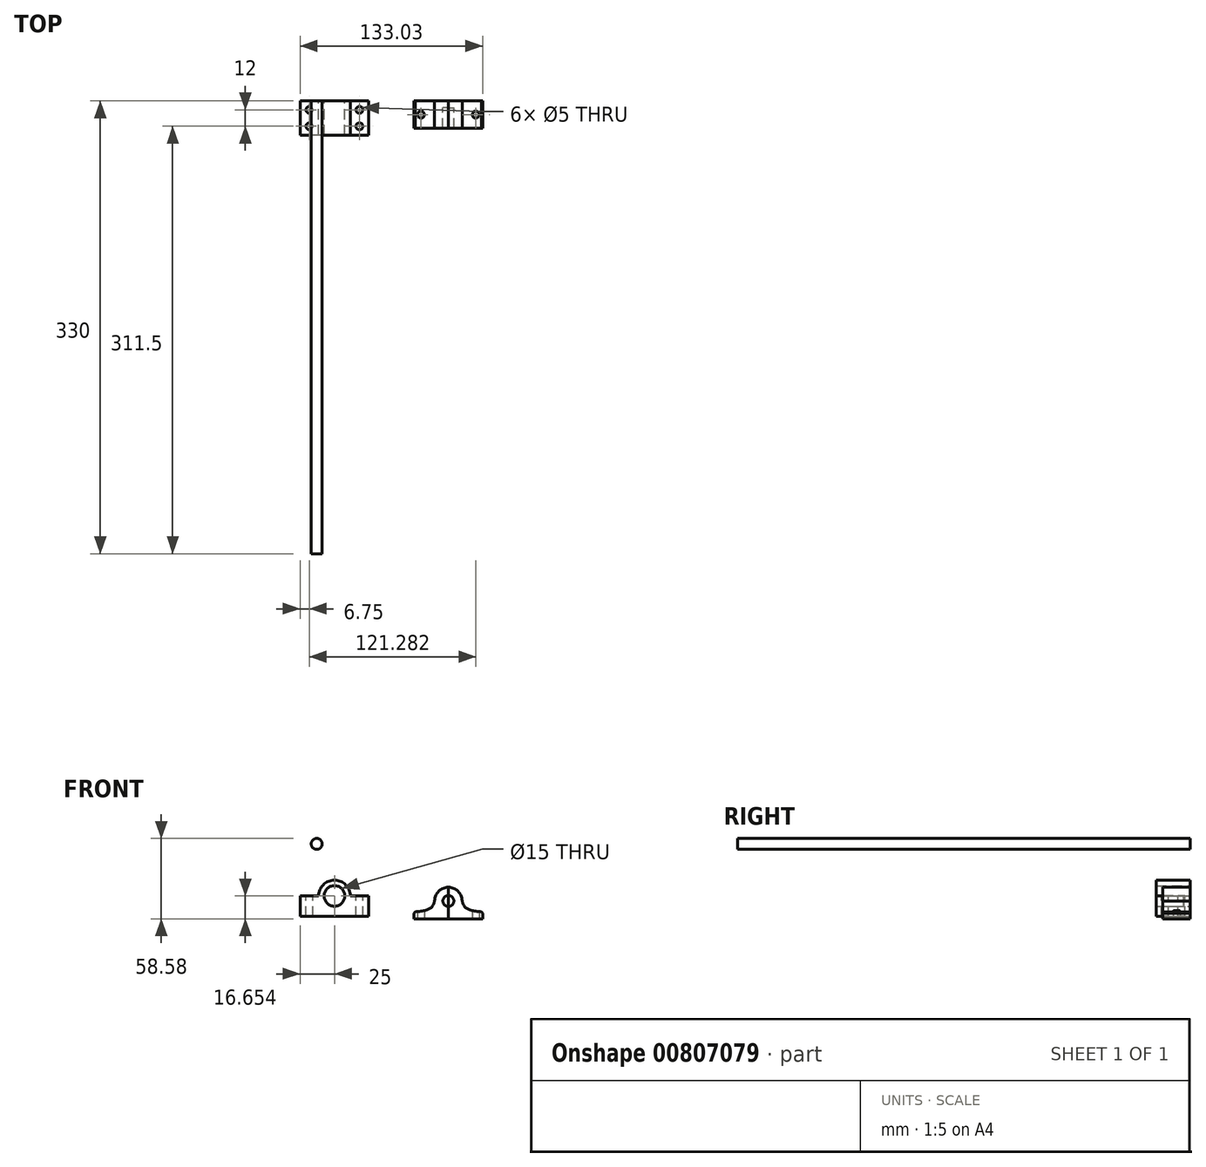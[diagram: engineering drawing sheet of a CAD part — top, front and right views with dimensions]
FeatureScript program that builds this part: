
annotation { "Feature Type Name" : "Feature", "Feature Type Description" : "" }
export const myFeature = defineFeature(function(context is Context, id is Id, definition is map)
    precondition{}
    {
        {
            var Q0;
            Q0=qCreatedBy(makeId("Front.planeOp"),FACE);
            var sketch = newSketch(context, id + "F0", { "sketchPlane" : qUnion([Q0])});
            skArc(sketch, "E0", {"start": v(-46.59, 23.73) * mm, "mid": v(-50.59, 19.73) * mm, "end": v(-46.59, 15.73) * mm});
            skArc(sketch, "E1", {"start": v(-46.59, 27.23) * mm, "mid": v(-54.09, 19.73) * mm, "end": v(-46.59, 12.23) * mm});
            skArc(sketch, "E2", {"start": v(-46.59, 31.23) * mm, "mid": v(-54.72, 27.87) * mm, "end": v(-58.09, 19.73) * mm});
            skLineSegment(sketch, "E3", {"start": v(-71.59, 19.73) * mm, "end": v(-71.59, 4.73) * mm});
            skLineSegment(sketch, "E4", {"start": v(-71.59, 4.73) * mm, "end": v(-46.59, 4.73) * mm});
            skLineSegment(sketch, "E5.trimOffspring", {"start": v(-58.09, 19.73) * mm, "end": v(-71.59, 19.73) * mm});
            skLineSegment(sketch, "E6", {"start": v(-46.59, 4.73) * mm, "end": v(-46.59, 12.23) * mm});
            skPoint(sketch, "E7.orphan", {"position": v(-21.59, 4.73) * mm});
            skLineSegment(sketch, "E8.trimOffspring", {"start": v(-46.59, 27.23) * mm, "end": v(-46.59, 31.23) * mm});
            skLineSegment(sketch, "E9", {"start": v(11.44, 3.08) * mm, "end": v(11.44, 8.08) * mm});
            skLineSegment(sketch, "E10", {"start": v(11.44, 3.08) * mm, "end": v(36.44, 3.08) * mm});
            skArc(sketch, "E11", {"start": v(36.44, 20.08) * mm, "mid": v(32.44, 16.08) * mm, "end": v(36.44, 12.08) * mm});
            skArc(sketch, "E12", {"start": v(36.44, 26.08) * mm, "mid": v(29.37, 23.15) * mm, "end": v(26.44, 16.08) * mm});
            skLineSegment(sketch, "E13", {"start": v(36.44, 3.08) * mm, "end": v(36.44, 12.08) * mm});
            skLineSegment(sketch, "E14.trimOffspring", {"start": v(36.44, 20.08) * mm, "end": v(36.44, 26.08) * mm});
            skFitSpline(sketch, "E15", {"points": [v(11.44, 8.08) * mm, v(23.62, 10.94) * mm, v(26.44, 16.08) * mm], "startDerivative": vector(24.53, 2.5) * mm, "endDerivative": vector(4.2, 14.23) * mm});
            skLineSegment(sketch, "E16", {"start": v(36.44, 12.08) * mm, "end": v(36.44, 20.08) * mm});
            skCircle(sketch, "E17", {"center": v(-59.52, 57.66) * mm, "radius": 4 * mm});
            skSolve(sketch);
        }
        {
            var Q0;
            Q0=makeQuery(id+"F0.imprint","IMPRINT",FACE,{"disambiguationData":[TD([[makeQuery(id+"F0.imprint","IMPRINT",EDGE,{"derivedFrom":sQuery(id+"F0.wireOp",EDGE,"E1")}),-1.0]])]});
            extrude(context, id + "F1", {"entities" : qUnion([Q0]), "depth" : 25 * mm, "offsetDistance" : 25 * mm});
        }
        {
            var Q0;
            Q0=makeQuery(id+"F1.opExtrude","SWEPT_FACE",FACE,{"disambiguationData":[OSD([sQuery(id+"F0.wireOp",EDGE,"E5.trimOffspring")])]});
            var sketch = newSketch(context, id + "F2", { "sketchPlane" : qUnion([Q0])});
            skCircle(sketch, "E18", {"center": v(-64.84, -6.5) * mm, "radius": 2.5 * mm});
            skCircle(sketch, "E19", {"center": v(-64.84, -18.5) * mm, "radius": 2.5 * mm});
            skSolve(sketch);
        }
        {
            var Q0;
            Q0=makeQuery(id+"F2.imprint","IMPRINT",FACE,{"disambiguationData":[TD([[makeQuery(id+"F2.imprint","IMPRINT",EDGE,{"derivedFrom":sQuery(id+"F2.wireOp",EDGE,"E18")}),1.0]])]});
            var Q1;
            Q1=makeQuery(id+"F2.imprint","IMPRINT",FACE,{"disambiguationData":[TD([[makeQuery(id+"F2.imprint","IMPRINT",EDGE,{"derivedFrom":sQuery(id+"F2.wireOp",EDGE,"E19")}),1.0]])]});
            extrude(context, id + "F3", {"entities" : qUnion([Q0, Q1]), "operationType" : NewBodyOperationType.REMOVE, "oppositeDirection" : true, "depth" : 25 * mm, "offsetDistance" : 25 * mm});
        }
        {
            var Q0;
            Q0=makeQuery(id+"F1.opExtrude","SWEPT_BODY",BODY,{"disambiguationData":[OSD([sQuery(id+"F0.wireOp",EDGE,"E1"),sQuery(id+"F0.wireOp",EDGE,"E2"),sQuery(id+"F0.wireOp",EDGE,"E3"),sQuery(id+"F0.wireOp",EDGE,"E4"),sQuery(id+"F0.wireOp",EDGE,"E5.trimOffspring"),sQuery(id+"F0.wireOp",EDGE,"E6"),sQuery(id+"F0.wireOp",EDGE,"E8.trimOffspring")])]});
            var Q1;
            Q1=makeQuery(id+"F1.opExtrude","SWEPT_FACE",FACE,{"disambiguationData":[OSD([sQuery(id+"F0.wireOp",EDGE,"E6")])]});
            mirror(context, id + "F4", {"operationType" : NewBodyOperationType.ADD, "entities" : qUnion([Q0]), "mirrorPlane" : qUnion([Q1])});
        }
        {
            var Q0;
            Q0=makeQuery(id+"F0.imprint","IMPRINT",FACE,{"disambiguationData":[TD([[makeQuery(id+"F0.imprint","IMPRINT",EDGE,{"derivedFrom":sQuery(id+"F0.wireOp",EDGE,"E9")}),-1.0]])]});
            extrude(context, id + "F5", {"entities" : qUnion([Q0]), "depth" : 20 * mm, "offsetDistance" : 25 * mm});
        }
        {
            var Q0;
            Q0=makeQuery(id+"F5.opExtrude","SWEPT_FACE",FACE,{"disambiguationData":[OSD([sQuery(id+"F0.wireOp",EDGE,"E10")])]});
            var sketch = newSketch(context, id + "F6", { "sketchPlane" : qUnion([Q0])});
            skPoint(sketch, "E20.startSnap0", {"position": v(11.44, 10) * mm});
            skCircle(sketch, "E21", {"center": v(16.44, 10) * mm, "radius": 2.5 * mm});
            skSolve(sketch);
        }
        {
            var Q0;
            Q0=makeQuery(id+"F6.imprint","IMPRINT",FACE,{"disambiguationData":[TD([[makeQuery(id+"F6.imprint","IMPRINT",EDGE,{"derivedFrom":sQuery(id+"F6.wireOp",EDGE,"E21")}),1.0]])]});
            extrude(context, id + "F7", {"entities" : qUnion([Q0]), "operationType" : NewBodyOperationType.REMOVE, "oppositeDirection" : true, "depth" : 10 * mm, "offsetDistance" : 25 * mm});
        }
        {
            var Q0;
            Q0=makeQuery(id+"F0.imprint","IMPRINT",FACE,{"disambiguationData":[TD([[makeQuery(id+"F0.imprint","IMPRINT",EDGE,{"derivedFrom":sQuery(id+"F0.wireOp",EDGE,"E11")}),1.0]])]});
            extrude(context, id + "F8", {"entities" : qUnion([Q0]), "operationType" : NewBodyOperationType.ADD, "depth" : 5 * mm, "offsetDistance" : 25 * mm});
        }
        {
            var Q0;
            Q0=makeQuery(id+"F5.opExtrude","SWEPT_EDGE",EDGE,{"disambiguationData":[OSD([sQuery(id+"F0.wireOp",EDGE,"E9"),sQuery(id+"F0.wireOp",EDGE,"E15")])]});
            chamfer(context, id + "F9", {"entities" : qUnion([Q0]), "width" : 1 * mm, "tangentPropagation" : true});
        }
        {
            var Q0;
            Q0=makeQuery(id+"F5.opExtrude","SWEPT_BODY",BODY,{"disambiguationData":[OSD([sQuery(id+"F0.wireOp",EDGE,"E9"),sQuery(id+"F0.wireOp",EDGE,"E10"),sQuery(id+"F0.wireOp",EDGE,"E11"),sQuery(id+"F0.wireOp",EDGE,"E12"),sQuery(id+"F0.wireOp",EDGE,"E13"),sQuery(id+"F0.wireOp",EDGE,"E14.trimOffspring"),sQuery(id+"F0.wireOp",EDGE,"E15")])]});
            var Q1;
            Q1=makeQuery(id+"F5.opExtrude","SWEPT_FACE",FACE,{"disambiguationData":[OSD([sQuery(id+"F0.wireOp",EDGE,"E13")])]});
            mirror(context, id + "F10", {"operationType" : NewBodyOperationType.ADD, "entities" : qUnion([Q0]), "mirrorPlane" : qUnion([Q1])});
        }
        {
            var Q0;
            Q0=makeQuery(id+"F0.imprint","IMPRINT",FACE,{"disambiguationData":[TD([[makeQuery(id+"F0.imprint","IMPRINT",EDGE,{"derivedFrom":sQuery(id+"F0.wireOp",EDGE,"E17")}),1.0]])]});
            extrude(context, id + "F11", {"entities" : qUnion([Q0]), "depth" : 330 * mm, "offsetDistance" : 25 * mm});
        }
    });
